# Revit family: Vitra-İntegra-TallUnit-62020+62021+62022+62023+62024+62025
name_source: partatom
category: Furniture Systems
revit_build: Autodesk Revit 2017 (Build: 20160225_1515(x64)
units: mm (PartAtom-declared; Revit-internal decimal feet)

## family parameters
Cut with Voids When Loaded = No
Host = Face
OmniClass Number = 23.40.00.00
OmniClass Title = Equipment and Furnishings
Part Type = Normal
Room Calculation Point = No
Round Connector Dimension = Use Diameter
Shared = Yes

## types (6) — shared parameters
BIMobject category = Storage
Construction Type = Wall Mounted
Default Elevation = 660 mm
Depth(mm) = 330 mm
Description = İntegra Tall Unit
Design country = Turkey
Height(mm) = 1600 mm  [stored 5.24934 ft]
IFC Classification = Furniture
Manufacturer = Vitra
Manufacturer name = Vitra
Masterformat 2014 Code = 12 35 30.23
Masterformat 2014 Description = Bathroom Casework
NBS Referans Code = 35-75-08
NBS Referans Description = Bathroom Cabinets
Nominal height = 0.000
Nominal width = 0.000
OmniClass Code = 23-31 25 13
OmniClass Description = Bathroom Cabinets
Product certification = https://vitraglobal.com
Product data url = https://www.vitraglobal.com
Product family = İntegra
Product group = Bathroom Furniture
Technical description = https://www.vitra.com.tr
Thrid Material = Vitra-AmericanValnut
UNSPSC Code = 30161801
UNSPSC Description = Bathroom Cabinets
URL = https://vitraglobal.com
Uniclass 1.4 Code = L8241
Uniclass 1.4 Description = Bathroom Cabinets
Uniclass 2.0 Code = PR-35-75-08
Uniclass 2.0 Description = Bathroom Cabinets
Uniclass 2015 Code = Pr_40_30_78_03
Uniclass 2015 Name = Bathroom Cabinets
Uniformat II Code = E2010
Uniformat II Description = Fixed Furnishings
Warranty Period (Year) = 2
Weight Net (kg) = 38,000
Width(mm) = 512 mm
Youtube = https://www.youtube.com

## per-type parameters (varying)
| type | Article No. (default) | Model | Primary Material | Product SKU | Secondary Material |
| TallUnit-Vitra-İntegra(Left)_62020 | 62020 | 62020 | Vitra-MattWhite | 62020 | Vitra-Bambu |
| TallUnit-Vitra-İntegra(Left)_62021 | 62021 | 62021 | Vitra-Kaşmir | 62021 | Vitra-MetalikCeviz |
| TallUnit-Vitra-İntegra(Left)_62022 | 62022 | 62022 | Vitra-Akçaağaç | 62022 | Vitra-Kumtaşı |
| TallUnit-Vitra-İntegra(Right)_62023 | 62023 | 62023 | Vitra-MattWhite | 62023 | Vitra-Bambu |
| TallUnit-Vitra-İntegra(Right)_62024 | 62024 | 62024 | Vitra-Kaşmir | 62024 | Vitra-MetalikCeviz |
| TallUnit-Vitra-İntegra(Right)_62025 | 62025 | 62025 | Vitra-Akçaağaç | 62025 | Vitra-Kumtaşı |

note: [stored X ft] marks values corroborated as IEEE doubles in the binary element streams (Revit-internal decimal feet)

## geometry (parser evidence)
native form markers: Sweep x3
no freeform markers — native parametric forms only
